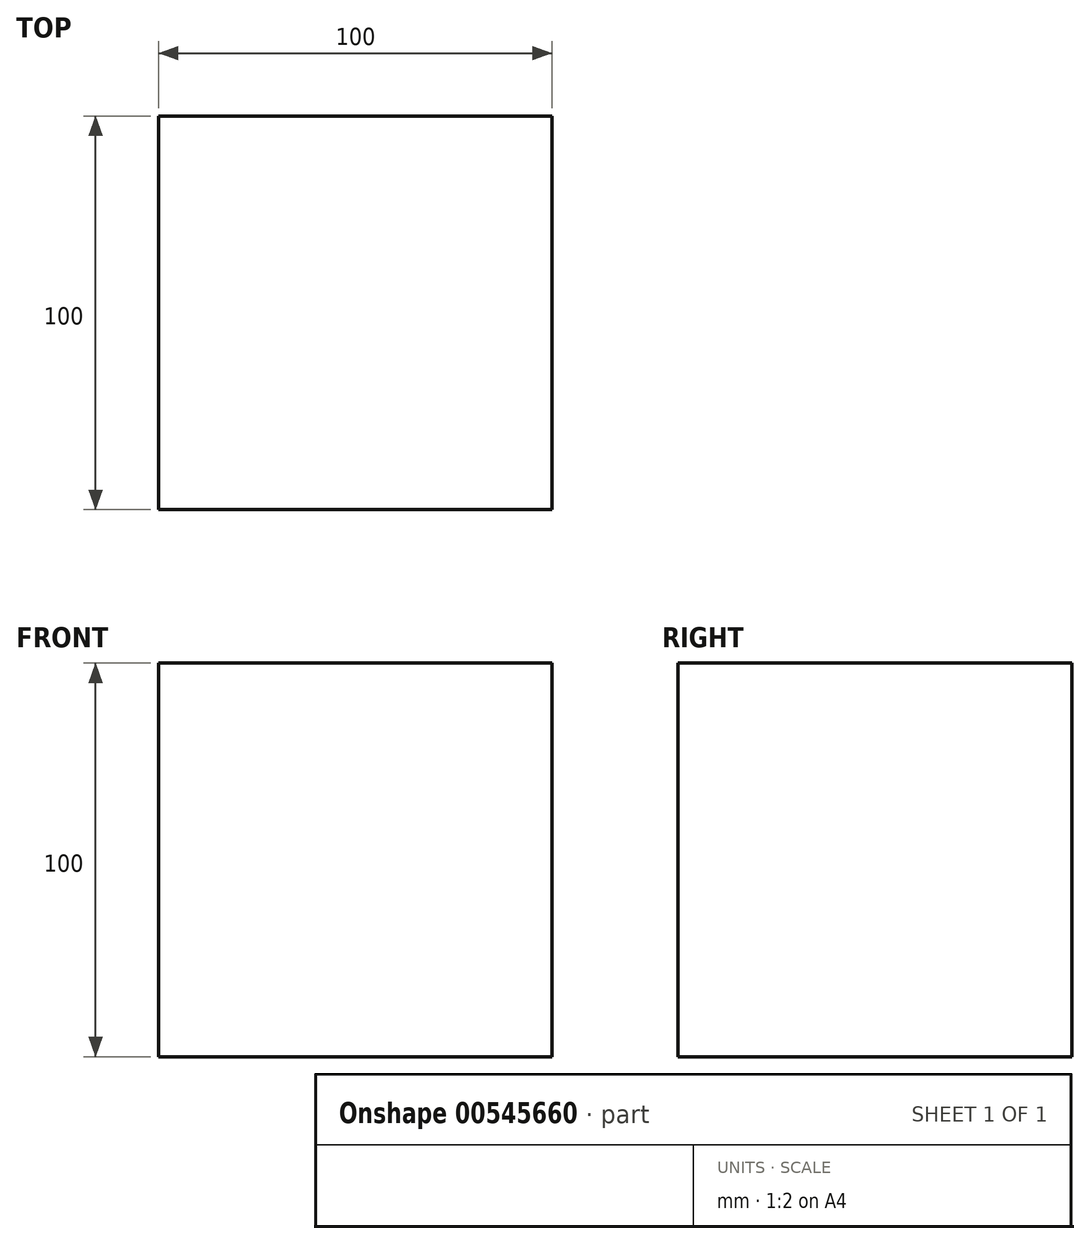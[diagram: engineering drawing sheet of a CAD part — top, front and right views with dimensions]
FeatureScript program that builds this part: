
annotation { "Feature Type Name" : "Feature", "Feature Type Description" : "" }
export const myFeature = defineFeature(function(context is Context, id is Id, definition is map)
    precondition{}
    {
        {
            var Q0;
            Q0=qCreatedBy(makeId("Front.planeOp"),FACE);
            var sketch = newSketch(context, id + "F0", { "sketchPlane" : qUnion([Q0])});
            skLineSegment(sketch, "E0.bottom", {"start": v(-50, 50) * mm, "end": v(50, 50) * mm});
            skLineSegment(sketch, "E0.top", {"start": v(-50, -50) * mm, "end": v(50, -50) * mm});
            skLineSegment(sketch, "E0.left", {"start": v(-50, 50) * mm, "end": v(-50, -50) * mm});
            skLineSegment(sketch, "E0.right", {"start": v(50, 50) * mm, "end": v(50, -50) * mm});
            skSolve(sketch);
        }
        {
            var Q0;
            Q0=makeQuery(id+"F0.imprint","IMPRINT",FACE,{"disambiguationData":[TD([[makeQuery(id+"F0.imprint","IMPRINT",EDGE,{"derivedFrom":sQuery(id+"F0.wireOp",EDGE,"E0.bottom")}),-1.0]])]});
            extrude(context, id + "F1", {"entities" : qUnion([Q0]), "depth" : 100 * mm, "offsetDistance" : 25 * mm});
        }
    });
